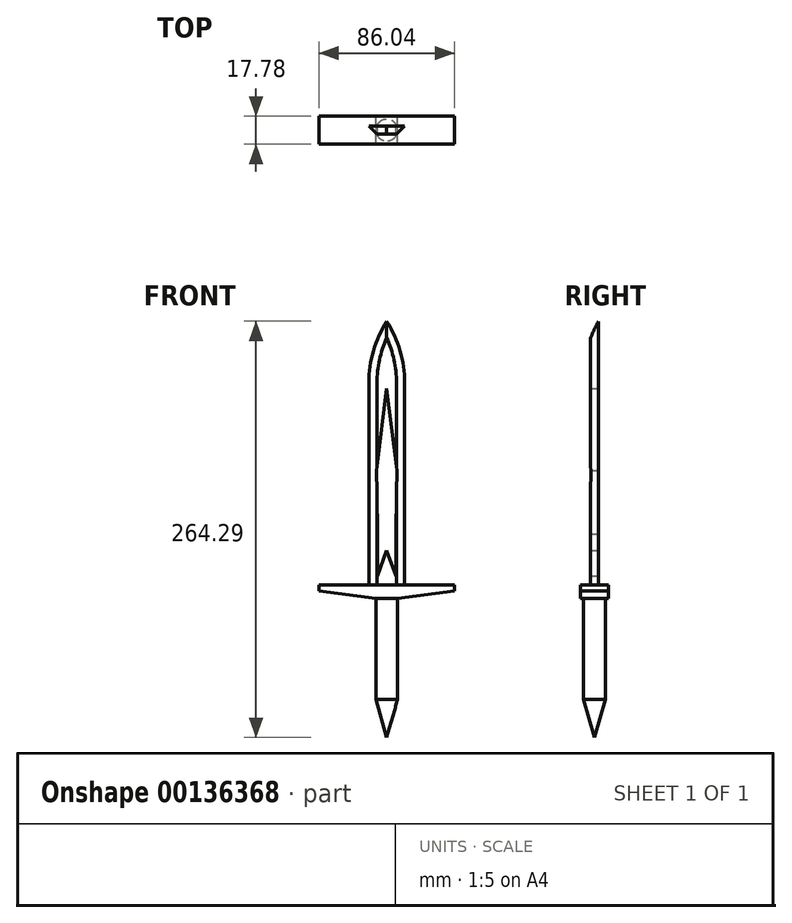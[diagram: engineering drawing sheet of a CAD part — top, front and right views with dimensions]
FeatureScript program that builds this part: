
annotation { "Feature Type Name" : "Feature", "Feature Type Description" : "" }
export const myFeature = defineFeature(function(context is Context, id is Id, definition is map)
    precondition{}
    {
        {
            var Q0;
            Q0=qCreatedBy(makeId("Front.planeOp"),FACE);
            var sketch = newSketch(context, id + "F0", { "sketchPlane" : qUnion([Q0])});
            skLineSegment(sketch, "E0", {"start": v(-6.9, 0) * mm, "end": v(-6.9, -64.23) * mm});
            skLineSegment(sketch, "E1", {"start": v(-6.9, -64.23) * mm, "end": v(0, -64.23) * mm});
            skLineSegment(sketch, "E2.MirrorCS", {"start": v(6.9, 0) * mm, "end": v(6.9, -64.23) * mm});
            skLineSegment(sketch, "E3.MirrorCS", {"start": v(6.9, -64.23) * mm, "end": v(0, -64.23) * mm});
            skLineSegment(sketch, "E4", {"start": v(-6.9, 0) * mm, "end": v(6.9, 0) * mm});
            skLineSegment(sketch, "E5", {"start": v(-6.9, 0) * mm, "end": v(-43.02, 4.56) * mm});
            skLineSegment(sketch, "E6", {"start": v(-43.02, 4.56) * mm, "end": v(-43.02, 8.4) * mm});
            skLineSegment(sketch, "E7", {"start": v(-43.02, 8.4) * mm, "end": v(0, 8.4) * mm});
            skLineSegment(sketch, "E8.MirrorCS", {"start": v(6.9, 0) * mm, "end": v(43.02, 4.56) * mm});
            skLineSegment(sketch, "E9.MirrorCS", {"start": v(43.02, 8.4) * mm, "end": v(0, 8.4) * mm});
            skLineSegment(sketch, "E10.MirrorCS", {"start": v(43.02, 4.56) * mm, "end": v(43.02, 8.4) * mm});
            skLineSegment(sketch, "E11", {"start": v(-11.32, 8.4) * mm, "end": v(-11.32, 136.83) * mm});
            skLineSegment(sketch, "E12.MirrorCS", {"start": v(11.32, 8.4) * mm, "end": v(11.32, 136.83) * mm});
            skArc(sketch, "E13", {"start": v(0, 175.93) * mm, "mid": v(-8.43, 157.18) * mm, "end": v(-11.32, 136.83) * mm});
            skArc(sketch, "E14.MirrorCS", {"start": v(0, 175.93) * mm, "mid": v(8.43, 157.18) * mm, "end": v(11.32, 136.83) * mm});
            skLineSegment(sketch, "E15", {"start": v(-6.53, 81.3) * mm, "end": v(0, 133.07) * mm});
            skLineSegment(sketch, "E16.MirrorCS", {"start": v(6.53, 81.3) * mm, "end": v(0, 133.07) * mm});
            skLineSegment(sketch, "E17", {"start": v(-6.53, 81.3) * mm, "end": v(-5.72, 40.85) * mm});
            skLineSegment(sketch, "E18", {"start": v(6.53, 81.3) * mm, "end": v(5.72, 40.85) * mm});
            skLineSegment(sketch, "E19", {"start": v(-5.72, 40.85) * mm, "end": v(-5.72, 14.05) * mm});
            skLineSegment(sketch, "E20", {"start": v(-5.72, 14.05) * mm, "end": v(0, 30.3) * mm});
            skLineSegment(sketch, "E21.MirrorCS", {"start": v(5.72, 14.05) * mm, "end": v(0, 30.3) * mm});
            skLineSegment(sketch, "E22.MirrorCS", {"start": v(5.72, 40.85) * mm, "end": v(5.72, 14.05) * mm});
            skLineSegment(sketch, "E23", {"start": v(0, 0) * mm, "end": v(0, -64.23) * mm});
            skLineSegment(sketch, "E24", {"start": v(-6.9, -64.23) * mm, "end": v(0, -88.36) * mm});
            skLineSegment(sketch, "E25", {"start": v(0, -88.36) * mm, "end": v(6.9, -64.23) * mm});
            skLineSegment(sketch, "E26", {"start": v(0, -88.36) * mm, "end": v(0, -64.23) * mm});
            skPoint(sketch, "E27", {"position": v(-4.2, 99.85) * mm});
            skPoint(sketch, "E28", {"position": v(4.2, 99.85) * mm});
            skSolve(sketch);
        }
        {
            var Q0;
            {var subQ0=sQuery(id+"F0.wireOp",EDGE,"E2.MirrorCS");Q0=makeQuery(id+"F0.imprint","IMPRINT",FACE,{"disambiguationData":[TD([[makeQuery(id+"F0.imprint","IMPRINT",EDGE,{"derivedFrom":subQ0}),-1.0]])]});}
            var Q1;
            Q1=sQuery(id+"F0.wireOp",EDGE,"E23");
            revolve(context, id + "F1", {"entities" : qUnion([Q0]), "axis" : qUnion([Q1]), "revolveType" : RevolveType.FULL});
        }
        {
            var Q0;
            Q0=makeQuery(id+"F0.imprint","IMPRINT",FACE,{"disambiguationData":[TD([[makeQuery(id+"F0.imprint","IMPRINT",EDGE,{"derivedFrom":sQuery(id+"F0.wireOp",EDGE,"E3.MirrorCS")}),1.0]])]});
            var Q1;
            Q1=sQuery(id+"F0.wireOp",EDGE,"E26");
            revolve(context, id + "F2", {"operationType" : NewBodyOperationType.ADD, "entities" : qUnion([Q0]), "axis" : qUnion([Q1]), "revolveType" : RevolveType.FULL});
        }
        {
            var Q0;
            {var subQ1=sQuery(id+"F0.wireOp",EDGE,"E5");Q0=makeQuery(id+"F0.imprint","IMPRINT",FACE,{"disambiguationData":[TD([[makeQuery(id+"F0.imprint","IMPRINT",EDGE,{"derivedFrom":subQ1}),-1.0]])]});}
            extrude(context, id + "F3", {"entities" : qUnion([Q0]), "endBound" : BoundingType.SYMMETRIC, "depth" : 17.78 * mm});
        }
        {
            var Q0;
            {var subQ0=sQuery(id+"F0.wireOp",EDGE,"E11");Q0=makeQuery(id+"F0.imprint","IMPRINT",FACE,{"disambiguationData":[TD([[makeQuery(id+"F0.imprint","IMPRINT",EDGE,{"derivedFrom":subQ0}),-1.0]])]});}
            extrude(context, id + "F4", {"entities" : qUnion([Q0]), "endBound" : BoundingType.SYMMETRIC, "depth" : 5.08 * mm});
        }
        {
            var Q0;
            Q0=makeQuery(id+"F4.opExtrude","CAP_EDGE",EDGE,{"disambiguationData":[OSD([sQuery(id+"F0.wireOp",EDGE,"E11")])],"isStart":false});
            var Q1;
            Q1=makeQuery(id+"F4.opExtrude","CAP_EDGE",EDGE,{"disambiguationData":[OSD([sQuery(id+"F0.wireOp",EDGE,"E12.MirrorCS")])],"isStart":false});
            chamfer(context, id + "F5", {"entities" : qUnion([Q0, Q1]), "width" : 5.08 * mm, "tangentPropagation" : true});
        }
    });
